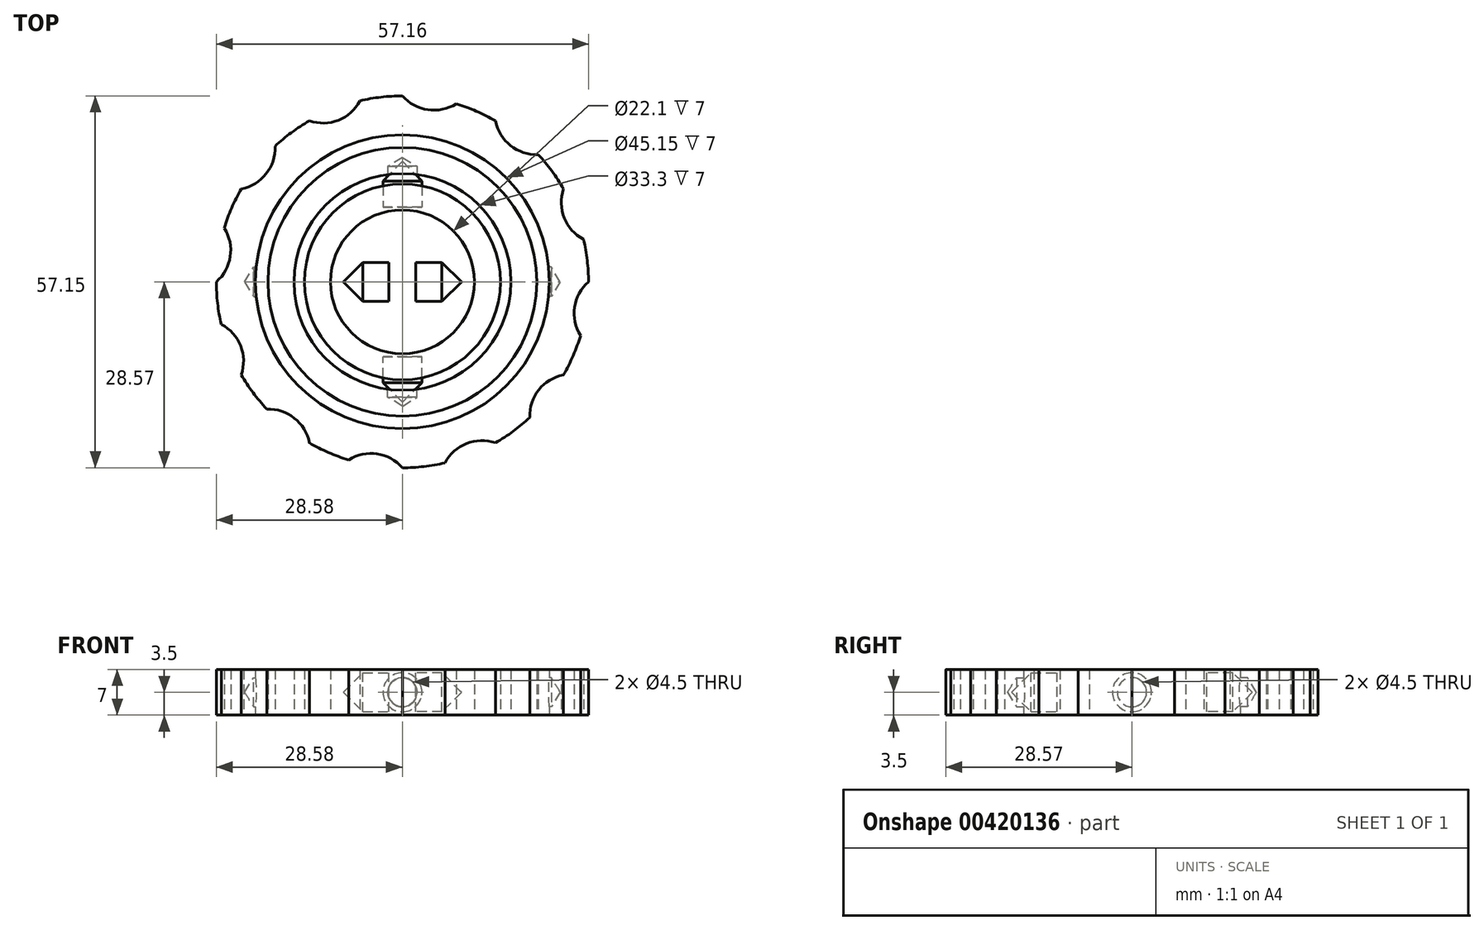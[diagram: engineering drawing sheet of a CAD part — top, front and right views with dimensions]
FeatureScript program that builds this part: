
annotation { "Feature Type Name" : "Feature", "Feature Type Description" : "" }
export const myFeature = defineFeature(function(context is Context, id is Id, definition is map)
    precondition{}
    {
        {
            var Q0;
            Q0=qCreatedBy(makeId("Top.planeOp"),FACE);
            var sketch = newSketch(context, id + "F0", { "sketchPlane" : qUnion([Q0])});
            skCircle(sketch, "E0", {"center": v(0, 0) * mm, "radius": 11.05 * mm});
            skCircle(sketch, "E1.0", {"center": v(0, 0) * mm, "radius": 15.05 * mm});
            skPoint(sketch, "E2", {"position": v(0, 15.05) * mm});
            skPoint(sketch, "E3", {"position": v(0, -15.05) * mm});
            skSolve(sketch);
        }
        {
            var Q0;
            Q0=makeQuery(id+"F0.imprint","IMPRINT",FACE,{"disambiguationData":[TD([[makeQuery(id+"F0.imprint","IMPRINT",EDGE,{"derivedFrom":sQuery(id+"F0.wireOp",EDGE,"E0")}),-1.0]])]});
            extrude(context, id + "F1", {"entities" : qUnion([Q0]), "endBound" : BoundingType.SYMMETRIC, "depth" : 7 * mm});
        }
        {
            var Q0;
            Q0=qCreatedBy(makeId("Front.planeOp"),FACE);
            cPlane(context, id + "F2", {"entities" : qUnion([Q0]), "cplaneType" : CPlaneType.OFFSET, "offset" : 11.5 * mm, "width" : 150 * mm, "height" : 150 * mm});
        }
        {
            var Q0;
            Q0=qCreatedBy(id+"F2.planeOp",FACE);
            var sketch = newSketch(context, id + "F3", { "sketchPlane" : qUnion([Q0])});
            skCircle(sketch, "E4", {"center": v(0, 0) * mm, "radius": 3 * mm});
            skSolve(sketch);
        }
        {
            var Q0;
            Q0 = qSketchRegion(id + "F3", true);
            extrude(context, id + "F4", {"entities" : qUnion([Q0]), "depth" : 7 * mm});
        }
        {
            var Q0;
            Q0=makeQuery(id+"F4.opExtrude","CAP_FACE",FACE,{"disambiguationData":[OSD([sQuery(id+"F3.wireOp",EDGE,"E4")])],"isStart":false});
            chamfer(context, id + "F5", {"entities" : qUnion([Q0]), "width" : 3 * mm, "tangentPropagation" : true});
        }
        {
            var Q0;
            Q0=qCreatedBy(makeId("Top.planeOp"),FACE);
            var sketch = newSketch(context, id + "F6", { "sketchPlane" : qUnion([Q0])});
            skCircle(sketch, "E5", {"center": v(0, 0) * mm, "radius": 16.65 * mm});
            skCircle(sketch, "E6.0", {"center": v(0, 0) * mm, "radius": 20.65 * mm});
            skSolve(sketch);
        }
        {
            var Q0;
            Q0=qCreatedBy(makeId("Front.planeOp"),FACE);
            cPlane(context, id + "F7", {"entities" : qUnion([Q0]), "cplaneType" : CPlaneType.OFFSET, "offset" : 16 * mm, "oppositeDirection" : true, "width" : 150 * mm, "height" : 150 * mm});
        }
        {
            var Q0;
            Q0=qCreatedBy(id+"F7.planeOp",FACE);
            var sketch = newSketch(context, id + "F8", { "sketchPlane" : qUnion([Q0])});
            skCircle(sketch, "E7", {"center": v(0, 0) * mm, "radius": 3 * mm});
            skSolve(sketch);
        }
        {
            var Q0;
            Q0=makeQuery(id+"F6.imprint","IMPRINT",FACE,{"disambiguationData":[TD([[makeQuery(id+"F6.imprint","IMPRINT",EDGE,{"derivedFrom":sQuery(id+"F6.wireOp",EDGE,"E5")}),-1.0]])]});
            extrude(context, id + "F9", {"entities" : qUnion([Q0]), "endBound" : BoundingType.SYMMETRIC, "depth" : 7 * mm});
        }
        {
            var Q0;
            Q0=makeQuery(id+"F4.opExtrude","SWEPT_BODY",BODY,{"disambiguationData":[OSD([sQuery(id+"F3.wireOp",EDGE,"E4")])]});
            var Q1;
            Q1=qCreatedBy(makeId("Front.planeOp"),FACE);
            mirror(context, id + "F10", {"entities" : qUnion([Q0]), "mirrorPlane" : qUnion([Q1])});
        }
        {
            var Q0;
            Q0=sQuery(id+"F8.wireOp",VERTEX,"E7.center");
            var Q1;
            Q1=makeQuery(id+"F9.opExtrude","SWEPT_BODY",BODY,{"disambiguationData":[OSD([sQuery(id+"F6.wireOp",EDGE,"E5"),sQuery(id+"F6.wireOp",EDGE,"E6.0")])]});
            hole(context, id + "F11", {"style" : HoleStyle.SIMPLE, "endStyle" : HoleEndStyle.BLIND, "holeDiameter" : 4.5 * mm, "holeDepth" : 1.1 * mm, "isTappedThrough" : true, "tappedDepth" : 12 * mm, "tapClearance" : 3, "locations" : qUnion([Q0]), "scope" : qUnion([Q1])});
        }
        {
            var Q0;
            Q0=qCreatedBy(makeId("Front.planeOp"),FACE);
            cPlane(context, id + "F12", {"entities" : qUnion([Q0]), "cplaneType" : CPlaneType.OFFSET, "offset" : 16 * mm, "width" : 150 * mm, "height" : 150 * mm});
        }
        {
            var Q0;
            Q0=qCreatedBy(id+"F12.planeOp",FACE);
            var sketch = newSketch(context, id + "F13", { "sketchPlane" : qUnion([Q0])});
            skCircle(sketch, "E8", {"center": v(0, 0) * mm, "radius": 2.72 * mm});
            skSolve(sketch);
        }
        {
            var Q0;
            Q0=sQuery(id+"F13.wireOp",VERTEX,"E8.center");
            var Q1;
            Q1=makeQuery(id+"F9.opExtrude","SWEPT_BODY",BODY,{"disambiguationData":[OSD([sQuery(id+"F6.wireOp",EDGE,"E5"),sQuery(id+"F6.wireOp",EDGE,"E6.0")])]});
            hole(context, id + "F14", {"style" : HoleStyle.SIMPLE, "endStyle" : HoleEndStyle.BLIND, "oppositeDirection" : true, "holeDiameter" : 4.5 * mm, "holeDepth" : 1.1 * mm, "isTappedThrough" : true, "tappedDepth" : 12 * mm, "tapClearance" : 3, "locations" : qUnion([Q0]), "scope" : qUnion([Q1])});
        }
        {
            var Q0;
            Q0=qCreatedBy(makeId("Right.planeOp"),FACE);
            cPlane(context, id + "F15", {"entities" : qUnion([Q0]), "cplaneType" : CPlaneType.OFFSET, "offset" : ((3.33 / 2) + .4) * mm, "width" : 150 * mm, "height" : 150 * mm});
        }
        {
            var Q0;
            Q0=qCreatedBy(id+"F15.planeOp",FACE);
            var sketch = newSketch(context, id + "F16", { "sketchPlane" : qUnion([Q0])});
            skCircle(sketch, "E9", {"center": v(0, 0) * mm, "radius": 3 * mm});
            skSolve(sketch);
        }
        {
            var Q0;
            Q0 = qSketchRegion(id + "F16", true);
            extrude(context, id + "F17", {"entities" : qUnion([Q0]), "depth" : 7 * mm});
        }
        {
            var Q0;
            Q0=makeQuery(id+"F17.opExtrude","CAP_FACE",FACE,{"disambiguationData":[OSD([sQuery(id+"F16.wireOp",EDGE,"E9")])],"isStart":false});
            chamfer(context, id + "F18", {"entities" : qUnion([Q0]), "width" : 3 * mm, "tangentPropagation" : true});
        }
        {
            var Q0;
            Q0=makeQuery(id+"F17.opExtrude","SWEPT_BODY",BODY,{"disambiguationData":[OSD([sQuery(id+"F16.wireOp",EDGE,"E9")])]});
            var Q1;
            Q1=qCreatedBy(makeId("Right.planeOp"),FACE);
            mirror(context, id + "F19", {"operationType" : NewBodyOperationType.ADD, "entities" : qUnion([Q0]), "mirrorPlane" : qUnion([Q1])});
        }
        {
            var Q0;
            Q0=qCreatedBy(makeId("Top.planeOp"),FACE);
            var sketch = newSketch(context, id + "F20", { "sketchPlane" : qUnion([Q0])});
            skCircle(sketch, "E10", {"center": v(0, 0) * mm, "radius": 22.57 * mm});
            skCircle(sketch, "E11.0", {"center": v(0, 0) * mm, "radius": 28.57 * mm});
            skArc(sketch, "E12", {"start": v(0, 28.57) * mm, "mid": v(3.9, 26.44) * mm, "end": v(8.26, 27.36) * mm});
            skArc(sketch, "E13.1.0", {"start": v(14.29, 24.75) * mm, "mid": v(16.6, 20.94) * mm, "end": v(20.83, 19.56) * mm});
            skArc(sketch, "E13.2.0", {"start": v(24.75, 14.29) * mm, "mid": v(24.84, 9.84) * mm, "end": v(27.82, 6.53) * mm});
            skArc(sketch, "E13.3.0", {"start": v(28.57, 0) * mm, "mid": v(26.44, -3.9) * mm, "end": v(27.36, -8.26) * mm});
            skArc(sketch, "E13.4.0", {"start": v(24.75, -14.29) * mm, "mid": v(20.94, -16.6) * mm, "end": v(19.56, -20.83) * mm});
            skArc(sketch, "E13.5.0", {"start": v(14.29, -24.75) * mm, "mid": v(9.84, -24.84) * mm, "end": v(6.53, -27.82) * mm});
            skArc(sketch, "E13.6.0", {"start": v(0, -28.57) * mm, "mid": v(-3.9, -26.44) * mm, "end": v(-8.26, -27.36) * mm});
            skArc(sketch, "E13.7.0", {"start": v(-14.29, -24.75) * mm, "mid": v(-16.6, -20.94) * mm, "end": v(-20.83, -19.56) * mm});
            skArc(sketch, "E13.8.0", {"start": v(-24.75, -14.29) * mm, "mid": v(-24.84, -9.84) * mm, "end": v(-27.82, -6.53) * mm});
            skArc(sketch, "E13.9.0", {"start": v(-28.57, 0) * mm, "mid": v(-26.44, 3.9) * mm, "end": v(-27.36, 8.26) * mm});
            skArc(sketch, "E13.10.0", {"start": v(-24.75, 14.29) * mm, "mid": v(-20.94, 16.6) * mm, "end": v(-19.56, 20.83) * mm});
            skArc(sketch, "E13.11.0", {"start": v(-14.29, 24.75) * mm, "mid": v(-9.84, 24.84) * mm, "end": v(-6.53, 27.82) * mm});
            skLineSegment(sketch, "E13.anchor1", {"start": v(0, 0) * mm, "end": v(0, 28.57) * mm, "construction": true});
            skLineSegment(sketch, "E13.anchor2", {"start": v(0, 0) * mm, "end": v(-14.29, 24.75) * mm, "construction": true});
            skSolve(sketch);
        }
        {
            var Q0;
            Q0=qCreatedBy(makeId("Right.planeOp"),FACE);
            cPlane(context, id + "F21", {"entities" : qUnion([Q0]), "cplaneType" : CPlaneType.OFFSET, "offset" : 22.1 * mm, "width" : 150 * mm, "height" : 150 * mm});
        }
        {
            var Q0;
            Q0=qCreatedBy(id+"F21.planeOp",FACE);
            var sketch = newSketch(context, id + "F22", { "sketchPlane" : qUnion([Q0])});
            skCircle(sketch, "E14", {"center": v(0, 0) * mm, "radius": 2.6 * mm});
            skSolve(sketch);
        }
        {
            var Q0;
            Q0=makeQuery(id+"F20.imprint","IMPRINT",FACE,{"disambiguationData":[TD([[makeQuery(id+"F20.imprint","IMPRINT",EDGE,{"derivedFrom":sQuery(id+"F20.wireOp",EDGE,"E10")}),-1.0]])]});
            extrude(context, id + "F23", {"entities" : qUnion([Q0]), "endBound" : BoundingType.SYMMETRIC, "depth" : 7 * mm});
        }
        {
            var Q0;
            Q0=sQuery(id+"F22.wireOp",VERTEX,"E14.center");
            var Q1;
            Q1=makeQuery(id+"F23.opExtrude","SWEPT_BODY",BODY,{"disambiguationData":[OSD([sQuery(id+"F20.wireOp",EDGE,"E10"),sQuery(id+"F20.wireOp",EDGE,"E11.0"),sQuery(id+"F20.wireOp",EDGE,"E12"),sQuery(id+"F20.wireOp",EDGE,"E13.1.0"),sQuery(id+"F20.wireOp",EDGE,"E13.2.0"),sQuery(id+"F20.wireOp",EDGE,"E13.3.0"),sQuery(id+"F20.wireOp",EDGE,"E13.4.0"),sQuery(id+"F20.wireOp",EDGE,"E13.5.0"),sQuery(id+"F20.wireOp",EDGE,"E13.6.0"),sQuery(id+"F20.wireOp",EDGE,"E13.7.0"),sQuery(id+"F20.wireOp",EDGE,"E13.8.0"),sQuery(id+"F20.wireOp",EDGE,"E13.9.0"),sQuery(id+"F20.wireOp",EDGE,"E13.10.0"),sQuery(id+"F20.wireOp",EDGE,"E13.11.0")])]});
            hole(context, id + "F24", {"style" : HoleStyle.SIMPLE, "endStyle" : HoleEndStyle.BLIND, "oppositeDirection" : true, "holeDiameter" : 4.5 * mm, "holeDepth" : 0.3 * mm, "isTappedThrough" : true, "tappedDepth" : 12 * mm, "tapClearance" : 3, "locations" : qUnion([Q0]), "scope" : qUnion([Q1])});
        }
        {
            var Q0;
            Q0=qCreatedBy(makeId("Right.planeOp"),FACE);
            cPlane(context, id + "F25", {"entities" : qUnion([Q0]), "cplaneType" : CPlaneType.OFFSET, "offset" : 22.1 * mm, "oppositeDirection" : true, "width" : 150 * mm, "height" : 150 * mm});
        }
        {
            var Q0;
            Q0=qCreatedBy(id+"F25.planeOp",FACE);
            var sketch = newSketch(context, id + "F26", { "sketchPlane" : qUnion([Q0])});
            skCircle(sketch, "E15", {"center": v(0, 0) * mm, "radius": 2.72 * mm});
            skSolve(sketch);
        }
        {
            var Q0;
            Q0=sQuery(id+"F26.wireOp",VERTEX,"E15.center");
            var Q1;
            Q1=makeQuery(id+"F23.opExtrude","SWEPT_BODY",BODY,{"disambiguationData":[OSD([sQuery(id+"F20.wireOp",EDGE,"E10"),sQuery(id+"F20.wireOp",EDGE,"E11.0"),sQuery(id+"F20.wireOp",EDGE,"E12"),sQuery(id+"F20.wireOp",EDGE,"E13.1.0"),sQuery(id+"F20.wireOp",EDGE,"E13.2.0"),sQuery(id+"F20.wireOp",EDGE,"E13.3.0"),sQuery(id+"F20.wireOp",EDGE,"E13.4.0"),sQuery(id+"F20.wireOp",EDGE,"E13.5.0"),sQuery(id+"F20.wireOp",EDGE,"E13.6.0"),sQuery(id+"F20.wireOp",EDGE,"E13.7.0"),sQuery(id+"F20.wireOp",EDGE,"E13.8.0"),sQuery(id+"F20.wireOp",EDGE,"E13.9.0"),sQuery(id+"F20.wireOp",EDGE,"E13.10.0"),sQuery(id+"F20.wireOp",EDGE,"E13.11.0")])]});
            hole(context, id + "F27", {"style" : HoleStyle.SIMPLE, "endStyle" : HoleEndStyle.BLIND, "holeDiameter" : 4.5 * mm, "holeDepth" : 0.3 * mm, "isTappedThrough" : true, "tappedDepth" : 12 * mm, "tapClearance" : 3, "locations" : qUnion([Q0]), "scope" : qUnion([Q1])});
        }
    });
